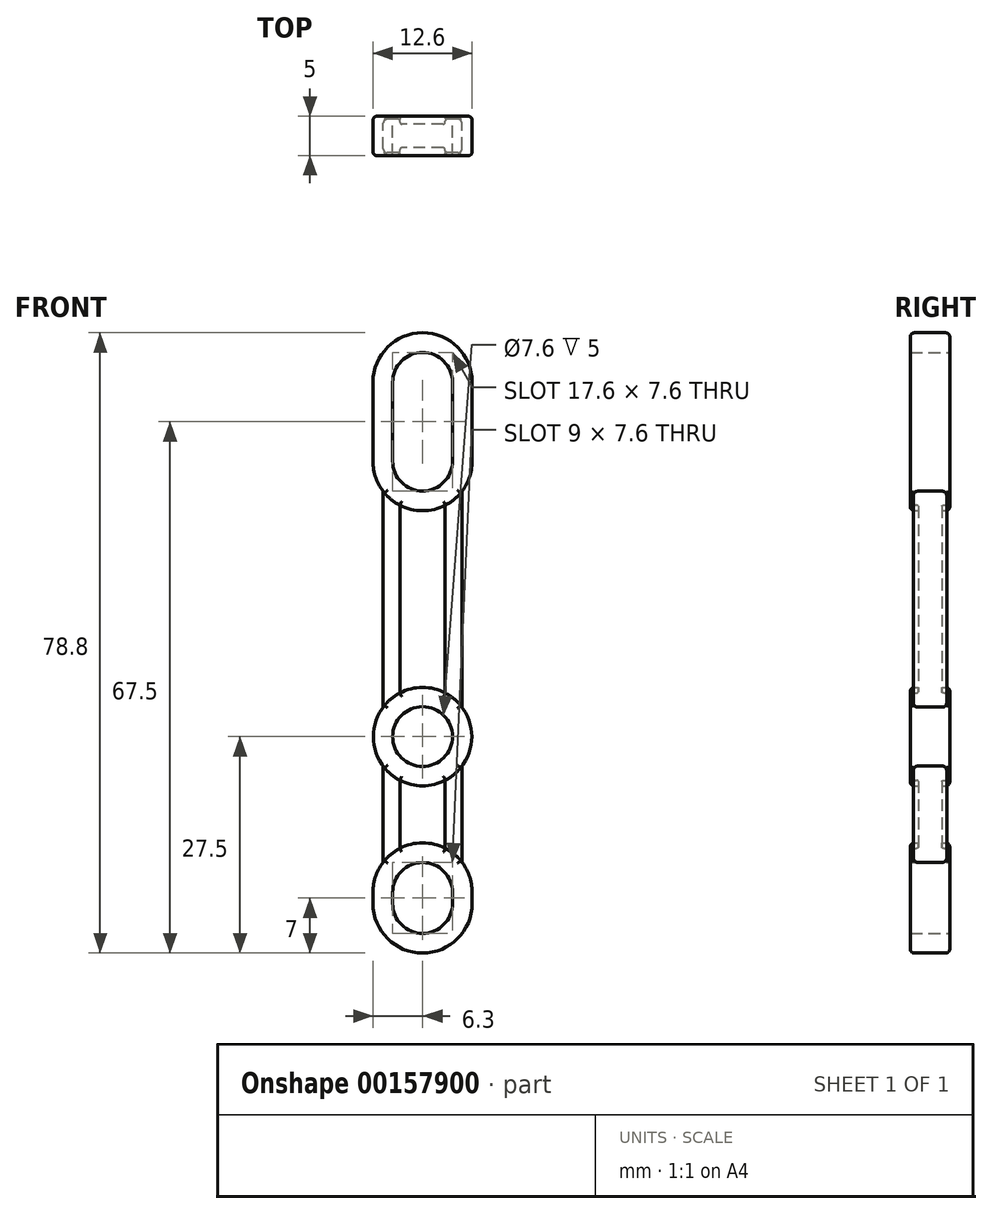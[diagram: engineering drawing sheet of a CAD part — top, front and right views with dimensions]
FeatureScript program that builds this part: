
annotation { "Feature Type Name" : "Feature", "Feature Type Description" : "" }
export const myFeature = defineFeature(function(context is Context, id is Id, definition is map)
    precondition{}
    {
        {
            var Q0;
            Q0=qCreatedBy(makeId("Front.planeOp"),FACE);
            var sketch = newSketch(context, id + "F0", { "sketchPlane" : qUnion([Q0])});
            skPoint(sketch, "E0.end.orphan", {"position": v(0, 40) * mm});
            skLineSegment(sketch, "E1.2", {"start": v(6.3, 45) * mm, "end": v(6.3, 35) * mm});
            skLineSegment(sketch, "E2", {"start": v(3.8, 45) * mm, "end": v(3.8, 35) * mm});
            skLineSegment(sketch, "E3.MirrorCS", {"start": v(-3.8, 45) * mm, "end": v(-3.8, 35) * mm});
            skLineSegment(sketch, "E4.MirrorCS", {"start": v(-6.3, 45) * mm, "end": v(-6.3, 35) * mm});
            skArc(sketch, "E5", {"start": v(-3.8, 35) * mm, "mid": v(0, 31.2) * mm, "end": v(3.8, 35) * mm});
            skArc(sketch, "E6", {"start": v(-6.3, 35) * mm, "mid": v(0, 28.7) * mm, "end": v(6.3, 35) * mm});
            skArc(sketch, "E7.MirrorCS", {"start": v(-6.3, 45) * mm, "mid": v(0, 51.3) * mm, "end": v(6.3, 45) * mm});
            skArc(sketch, "E8.MirrorCS", {"start": v(-3.8, 45) * mm, "mid": v(0, 48.8) * mm, "end": v(3.8, 45) * mm});
            skCircle(sketch, "E9", {"center": v(0, 0) * mm, "radius": 3.8 * mm});
            skCircle(sketch, "E10", {"center": v(0, 0) * mm, "radius": 6.25 * mm});
            skSolve(sketch);
        }
        {
            var Q0;
            Q0=makeQuery(id+"F0.imprint","IMPRINT",FACE,{"disambiguationData":[TD([[makeQuery(id+"F0.imprint","IMPRINT",EDGE,{"derivedFrom":sQuery(id+"F0.wireOp",EDGE,"E1.2")}),-1.0]])]});
            extrude(context, id + "F1", {"entities" : qUnion([Q0]), "depth" : 5 * mm, "symmetric" : true});
        }
        {
            var Q0;
            Q0=qCreatedBy(makeId("Front.planeOp"),FACE);
            var sketch = newSketch(context, id + "F2", { "sketchPlane" : qUnion([Q0])});
            skCircle(sketch, "E11", {"center": v(0, 0) * mm, "radius": 3.8 * mm});
            skCircle(sketch, "E12", {"center": v(0, 0) * mm, "radius": 6.25 * mm});
            skSolve(sketch);
        }
        {
            var Q0;
            Q0 = qSketchRegion(id + "F2", true);
            extrude(context, id + "F3", {"entities" : qUnion([Q0]), "operationType" : NewBodyOperationType.ADD, "depth" : 5 * mm, "symmetric" : true});
        }
        {
            var Q0;
            Q0=qCreatedBy(makeId("Front.planeOp"),FACE);
            var sketch = newSketch(context, id + "F4", { "sketchPlane" : qUnion([Q0])});
            skArc(sketch, "E13", {"start": v(-3.8, -21.2) * mm, "mid": v(0, -25) * mm, "end": v(3.8, -21.2) * mm});
            skLineSegment(sketch, "E14", {"start": v(0, -19.8) * mm, "end": v(0, -20) * mm});
            skLineSegment(sketch, "E15", {"start": v(0, -20) * mm, "end": v(0, -21.2) * mm});
            skArc(sketch, "E16.trimOffspring", {"start": v(3.8, -19.8) * mm, "mid": v(0, -16) * mm, "end": v(-3.8, -19.8) * mm});
            skLineSegment(sketch, "E17", {"start": v(-3.8, -19.8) * mm, "end": v(-3.8, -21.2) * mm});
            skLineSegment(sketch, "E18", {"start": v(3.8, -19.8) * mm, "end": v(3.8, -21.2) * mm});
            skLineSegment(sketch, "E19.0", {"start": v(-6.3, -19.8) * mm, "end": v(-6.3, -21.2) * mm});
            skArc(sketch, "E19.1", {"start": v(6.3, -19.8) * mm, "mid": v(0, -13.5) * mm, "end": v(-6.3, -19.8) * mm});
            skLineSegment(sketch, "E19.2", {"start": v(6.3, -19.8) * mm, "end": v(6.3, -21.2) * mm});
            skArc(sketch, "E19.3", {"start": v(-6.3, -21.2) * mm, "mid": v(0, -27.5) * mm, "end": v(6.3, -21.2) * mm});
            skSolve(sketch);
        }
        {
            var Q0;
            Q0 = qSketchRegion(id + "F4", true);
            extrude(context, id + "F5", {"entities" : qUnion([Q0]), "operationType" : NewBodyOperationType.ADD, "depth" : 5 * mm, "symmetric" : true});
        }
        {
            var Q0;
            Q0=qCreatedBy(makeId("Top.planeOp"),FACE);
            cPlane(context, id + "F6", {"entities" : qUnion([Q0]), "cplaneType" : CPlaneType.OFFSET, "offset" : 20 * mm, "width" : 150 * mm, "height" : 150 * mm});
        }
        {
            var Q0;
            Q0=qCreatedBy(id+"F6.planeOp",FACE);
            var sketch = newSketch(context, id + "F7", { "sketchPlane" : qUnion([Q0])});
            skLineSegment(sketch, "E20.top", {"start": v(-4.5, 2.12) * mm, "end": v(-3.12, 2.12) * mm});
            skLineSegment(sketch, "E21", {"start": v(5, -1.63) * mm, "end": v(5, 1.62) * mm});
            skLineSegment(sketch, "E22", {"start": v(-5, -1.63) * mm, "end": v(-5, 1.62) * mm});
            skLineSegment(sketch, "E23", {"start": v(-4.5, -2.13) * mm, "end": v(-3.12, -2.13) * mm});
            skLineSegment(sketch, "E24.bottom", {"start": v(-2.62, -1.5) * mm, "end": v(2.62, -1.5) * mm});
            skLineSegment(sketch, "E24.top", {"start": v(-2.63, 1.5) * mm, "end": v(2.62, 1.5) * mm});
            skLineSegment(sketch, "E25", {"start": v(-2.88, -1.75) * mm, "end": v(-2.88, -1.88) * mm});
            skLineSegment(sketch, "E26", {"start": v(-2.88, 1.75) * mm, "end": v(-2.88, 1.87) * mm});
            skLineSegment(sketch, "E27", {"start": v(2.87, 1.75) * mm, "end": v(2.87, 1.87) * mm});
            skLineSegment(sketch, "E28", {"start": v(2.88, -1.75) * mm, "end": v(2.88, -1.88) * mm});
            skLineSegment(sketch, "E29.trimOffspring", {"start": v(3.12, -2.13) * mm, "end": v(4.5, -2.13) * mm});
            skLineSegment(sketch, "E30.trimOffspring", {"start": v(3.12, 2.12) * mm, "end": v(4.5, 2.12) * mm});
            skPoint(sketch, "E31.visualSharp", {"position": v(-5, -2.13) * mm});
            skArc(sketch, "E31.filletArc", {"start": v(-5, -1.63) * mm, "mid": v(-4.85, -1.98) * mm, "end": v(-4.5, -2.13) * mm});
            skPoint(sketch, "E32.visualSharp", {"position": v(-5, 2.12) * mm});
            skArc(sketch, "E32.filletArc", {"start": v(-4.5, 2.12) * mm, "mid": v(-4.85, 1.98) * mm, "end": v(-5, 1.62) * mm});
            skPoint(sketch, "E33.visualSharp", {"position": v(5, 2.13) * mm});
            skArc(sketch, "E33.filletArc", {"start": v(5, 1.62) * mm, "mid": v(4.85, 1.98) * mm, "end": v(4.5, 2.12) * mm});
            skPoint(sketch, "E34.visualSharp", {"position": v(5, -2.13) * mm});
            skArc(sketch, "E34.filletArc", {"start": v(4.5, -2.13) * mm, "mid": v(4.85, -1.98) * mm, "end": v(5, -1.63) * mm});
            skPoint(sketch, "E35.visualSharp", {"position": v(2.88, -1.5) * mm});
            skArc(sketch, "E35.filletArc", {"start": v(2.88, -1.75) * mm, "mid": v(2.8, -1.57) * mm, "end": v(2.62, -1.5) * mm});
            skPoint(sketch, "E36.visualSharp", {"position": v(-2.88, -1.5) * mm});
            skArc(sketch, "E36.filletArc", {"start": v(-2.62, -1.5) * mm, "mid": v(-2.8, -1.57) * mm, "end": v(-2.88, -1.75) * mm});
            skPoint(sketch, "E37.visualSharp", {"position": v(-2.88, 1.5) * mm});
            skArc(sketch, "E37.filletArc", {"start": v(-2.88, 1.75) * mm, "mid": v(-2.8, 1.57) * mm, "end": v(-2.63, 1.5) * mm});
            skPoint(sketch, "E38.visualSharp", {"position": v(2.87, 1.5) * mm});
            skArc(sketch, "E38.filletArc", {"start": v(2.62, 1.5) * mm, "mid": v(2.8, 1.57) * mm, "end": v(2.88, 1.75) * mm});
            skPoint(sketch, "E39.visualSharp", {"position": v(2.88, -2.13) * mm});
            skArc(sketch, "E39.filletArc", {"start": v(2.88, -1.88) * mm, "mid": v(2.95, -2.05) * mm, "end": v(3.12, -2.13) * mm});
            skPoint(sketch, "E40.visualSharp", {"position": v(-2.88, -2.13) * mm});
            skArc(sketch, "E40.filletArc", {"start": v(-3.12, -2.13) * mm, "mid": v(-2.95, -2.05) * mm, "end": v(-2.88, -1.88) * mm});
            skPoint(sketch, "E41.visualSharp", {"position": v(-2.88, 2.12) * mm});
            skArc(sketch, "E41.filletArc", {"start": v(-2.88, 1.87) * mm, "mid": v(-2.95, 2.05) * mm, "end": v(-3.12, 2.12) * mm});
            skPoint(sketch, "E42.visualSharp", {"position": v(2.87, 2.12) * mm});
            skArc(sketch, "E42.filletArc", {"start": v(3.12, 2.12) * mm, "mid": v(2.95, 2.05) * mm, "end": v(2.87, 1.87) * mm});
            skSolve(sketch);
        }
        {
            var Q0;
            Q0=makeQuery(id+"F7.imprint","IMPRINT",FACE,{"disambiguationData":[TD([[makeQuery(id+"F7.imprint","IMPRINT",EDGE,{"derivedFrom":sQuery(id+"F7.wireOp",EDGE,"E20.top")}),-1.0]])]});
            var Q1;
            Q1=makeQuery(id+"F1.opExtrude","SWEPT_BODY",BODY,{"disambiguationData":[OSD([sQuery(id+"F0.wireOp",EDGE,"E1.2"),sQuery(id+"F0.wireOp",EDGE,"E2"),sQuery(id+"F0.wireOp",EDGE,"E3.MirrorCS"),sQuery(id+"F0.wireOp",EDGE,"E4.MirrorCS"),sQuery(id+"F0.wireOp",EDGE,"E5"),sQuery(id+"F0.wireOp",EDGE,"E6"),sQuery(id+"F0.wireOp",EDGE,"E7.MirrorCS"),sQuery(id+"F0.wireOp",EDGE,"E8.MirrorCS")])]});
            extrude(context, id + "F8", {"entities" : qUnion([Q0]), "operationType" : NewBodyOperationType.ADD, "endBound" : BoundingType.UP_TO_BODY, "endBoundEntityBody" : qUnion([Q1]), "depth" : 25 * mm});
        }
        {
            var Q0;
            Q0=makeQuery(id+"F8.opExtrude","CAP_FACE",FACE,{"disambiguationData":[OSD([sQuery(id+"F7.wireOp",EDGE,"E20.top"),sQuery(id+"F7.wireOp",EDGE,"E21"),sQuery(id+"F7.wireOp",EDGE,"E22"),sQuery(id+"F7.wireOp",EDGE,"E23"),sQuery(id+"F7.wireOp",EDGE,"E24.bottom"),sQuery(id+"F7.wireOp",EDGE,"E24.top"),sQuery(id+"F7.wireOp",EDGE,"E25"),sQuery(id+"F7.wireOp",EDGE,"E26"),sQuery(id+"F7.wireOp",EDGE,"E27"),sQuery(id+"F7.wireOp",EDGE,"E28"),sQuery(id+"F7.wireOp",EDGE,"E29.trimOffspring"),sQuery(id+"F7.wireOp",EDGE,"E30.trimOffspring"),sQuery(id+"F7.wireOp",EDGE,"E31.filletArc"),sQuery(id+"F7.wireOp",EDGE,"E32.filletArc"),sQuery(id+"F7.wireOp",EDGE,"E33.filletArc"),sQuery(id+"F7.wireOp",EDGE,"E34.filletArc"),sQuery(id+"F7.wireOp",EDGE,"E35.filletArc"),sQuery(id+"F7.wireOp",EDGE,"E36.filletArc"),sQuery(id+"F7.wireOp",EDGE,"E37.filletArc"),sQuery(id+"F7.wireOp",EDGE,"E38.filletArc"),sQuery(id+"F7.wireOp",EDGE,"E39.filletArc"),sQuery(id+"F7.wireOp",EDGE,"E40.filletArc"),sQuery(id+"F7.wireOp",EDGE,"E41.filletArc"),sQuery(id+"F7.wireOp",EDGE,"E42.filletArc")])],"isStart":true});
            var Q1;
            Q1=makeQuery(id+"F3.opExtrude","SWEPT_BODY",BODY,{"disambiguationData":[OSD([sQuery(id+"F2.wireOp",EDGE,"E11"),sQuery(id+"F2.wireOp",EDGE,"E12")])]});
            extrude(context, id + "F9", {"entities" : qUnion([Q0]), "operationType" : NewBodyOperationType.ADD, "endBound" : BoundingType.UP_TO_BODY, "endBoundEntityBody" : qUnion([Q1]), "depth" : 25 * mm});
        }
        {
            var Q0;
            Q0=qCreatedBy(makeId("Top.planeOp"),FACE);
            cPlane(context, id + "F10", {"entities" : qUnion([Q0]), "cplaneType" : CPlaneType.OFFSET, "offset" : 10 * mm, "oppositeDirection" : true, "width" : 150 * mm, "height" : 150 * mm});
        }
        {
            var Q0;
            Q0=qCreatedBy(id+"F10.planeOp",FACE);
            var sketch = newSketch(context, id + "F11", { "sketchPlane" : qUnion([Q0])});
            skLineSegment(sketch, "E43.0", {"start": v(-4.5, 2.12) * mm, "end": v(-3.12, 2.12) * mm});
            skLineSegment(sketch, "E43.1", {"start": v(5, -1.63) * mm, "end": v(5, 1.62) * mm});
            skLineSegment(sketch, "E43.2", {"start": v(-5, -1.63) * mm, "end": v(-5, 1.62) * mm});
            skLineSegment(sketch, "E43.3", {"start": v(-4.5, -2.13) * mm, "end": v(-3.12, -2.13) * mm});
            skLineSegment(sketch, "E43.4", {"start": v(-2.62, -1.5) * mm, "end": v(2.62, -1.5) * mm});
            skLineSegment(sketch, "E43.5", {"start": v(-2.63, 1.5) * mm, "end": v(2.62, 1.5) * mm});
            skLineSegment(sketch, "E43.6", {"start": v(-2.88, -1.75) * mm, "end": v(-2.88, -1.88) * mm});
            skLineSegment(sketch, "E43.7", {"start": v(-2.88, 1.75) * mm, "end": v(-2.88, 1.87) * mm});
            skLineSegment(sketch, "E43.8", {"start": v(2.87, 1.75) * mm, "end": v(2.87, 1.87) * mm});
            skLineSegment(sketch, "E43.9", {"start": v(2.88, -1.75) * mm, "end": v(2.88, -1.88) * mm});
            skLineSegment(sketch, "E43.10", {"start": v(3.12, -2.13) * mm, "end": v(4.5, -2.13) * mm});
            skLineSegment(sketch, "E43.11", {"start": v(3.12, 2.12) * mm, "end": v(4.5, 2.12) * mm});
            skPoint(sketch, "E43.12", {"position": v(-5, -2.13) * mm});
            skArc(sketch, "E43.13", {"start": v(-5, -1.63) * mm, "mid": v(-4.85, -1.98) * mm, "end": v(-4.5, -2.13) * mm});
            skPoint(sketch, "E43.14", {"position": v(-5, 2.12) * mm});
            skArc(sketch, "E43.15", {"start": v(-4.5, 2.12) * mm, "mid": v(-4.85, 1.98) * mm, "end": v(-5, 1.62) * mm});
            skPoint(sketch, "E43.16", {"position": v(5, 2.13) * mm});
            skArc(sketch, "E43.17", {"start": v(5, 1.62) * mm, "mid": v(4.85, 1.98) * mm, "end": v(4.5, 2.12) * mm});
            skPoint(sketch, "E43.18", {"position": v(5, -2.13) * mm});
            skArc(sketch, "E43.19", {"start": v(4.5, -2.13) * mm, "mid": v(4.85, -1.98) * mm, "end": v(5, -1.63) * mm});
            skPoint(sketch, "E43.20", {"position": v(2.88, -1.5) * mm});
            skArc(sketch, "E43.21", {"start": v(2.88, -1.75) * mm, "mid": v(2.8, -1.57) * mm, "end": v(2.62, -1.5) * mm});
            skPoint(sketch, "E43.22", {"position": v(-2.88, -1.5) * mm});
            skArc(sketch, "E43.23", {"start": v(-2.62, -1.5) * mm, "mid": v(-2.8, -1.57) * mm, "end": v(-2.88, -1.75) * mm});
            skPoint(sketch, "E43.24", {"position": v(-2.88, 1.5) * mm});
            skArc(sketch, "E43.25", {"start": v(-2.88, 1.75) * mm, "mid": v(-2.8, 1.57) * mm, "end": v(-2.63, 1.5) * mm});
            skPoint(sketch, "E43.26", {"position": v(2.87, 1.5) * mm});
            skArc(sketch, "E43.27", {"start": v(2.62, 1.5) * mm, "mid": v(2.8, 1.57) * mm, "end": v(2.88, 1.75) * mm});
            skPoint(sketch, "E43.28", {"position": v(2.88, -2.13) * mm});
            skArc(sketch, "E43.29", {"start": v(2.88, -1.88) * mm, "mid": v(2.95, -2.05) * mm, "end": v(3.12, -2.13) * mm});
            skPoint(sketch, "E43.30", {"position": v(-2.88, -2.13) * mm});
            skArc(sketch, "E43.31", {"start": v(-3.12, -2.13) * mm, "mid": v(-2.95, -2.05) * mm, "end": v(-2.88, -1.88) * mm});
            skPoint(sketch, "E43.32", {"position": v(-2.88, 2.12) * mm});
            skArc(sketch, "E43.33", {"start": v(-2.88, 1.87) * mm, "mid": v(-2.95, 2.05) * mm, "end": v(-3.12, 2.12) * mm});
            skPoint(sketch, "E43.34", {"position": v(2.87, 2.12) * mm});
            skArc(sketch, "E43.35", {"start": v(3.12, 2.12) * mm, "mid": v(2.95, 2.05) * mm, "end": v(2.87, 1.87) * mm});
            skLineSegment(sketch, "E43.36", {"start": v(-2.62, -1.5) * mm, "end": v(2.62, -1.5) * mm});
            skSolve(sketch);
        }
        {
            var Q0;
            Q0 = qSketchRegion(id + "F11", true);
            var Q1;
            Q1=makeQuery(id+"F3.opExtrude","SWEPT_FACE",FACE,{"disambiguationData":[OSD([sQuery(id+"F2.wireOp",EDGE,"E12")])]});
            var Q2;
            Q2=makeQuery(id+"F3.opExtrude","SWEPT_BODY",BODY,{"disambiguationData":[OSD([sQuery(id+"F2.wireOp",EDGE,"E11"),sQuery(id+"F2.wireOp",EDGE,"E12")])]});
            extrude(context, id + "F12", {"entities" : qUnion([Q0]), "operationType" : NewBodyOperationType.ADD, "endBound" : BoundingType.UP_TO_SURFACE, "endBoundEntityFace" : qUnion([Q1]), "endBoundEntityBody" : qUnion([Q2]), "depth" : 25 * mm});
        }
        {
            var Q0;
            Q0=makeQuery(id+"F12.opExtrude","CAP_FACE",FACE,{"disambiguationData":[OSD([sQuery(id+"F11.wireOp",EDGE,"E43.0"),sQuery(id+"F11.wireOp",EDGE,"E43.1"),sQuery(id+"F11.wireOp",EDGE,"E43.2"),sQuery(id+"F11.wireOp",EDGE,"E43.3"),sQuery(id+"F11.wireOp",EDGE,"E43.5"),sQuery(id+"F11.wireOp",EDGE,"E43.6"),sQuery(id+"F11.wireOp",EDGE,"E43.7"),sQuery(id+"F11.wireOp",EDGE,"E43.8"),sQuery(id+"F11.wireOp",EDGE,"E43.9"),sQuery(id+"F11.wireOp",EDGE,"E43.10"),sQuery(id+"F11.wireOp",EDGE,"E43.11"),sQuery(id+"F11.wireOp",EDGE,"E43.13"),sQuery(id+"F11.wireOp",EDGE,"E43.15"),sQuery(id+"F11.wireOp",EDGE,"E43.17"),sQuery(id+"F11.wireOp",EDGE,"E43.19"),sQuery(id+"F11.wireOp",EDGE,"E43.21"),sQuery(id+"F11.wireOp",EDGE,"E43.23"),sQuery(id+"F11.wireOp",EDGE,"E43.25"),sQuery(id+"F11.wireOp",EDGE,"E43.27"),sQuery(id+"F11.wireOp",EDGE,"E43.29"),sQuery(id+"F11.wireOp",EDGE,"E43.31"),sQuery(id+"F11.wireOp",EDGE,"E43.33"),sQuery(id+"F11.wireOp",EDGE,"E43.35"),sQuery(id+"F11.wireOp",EDGE,"E43.36")])],"isStart":true});
            var Q1;
            Q1=makeQuery(id+"F5.opExtrude","SWEPT_BODY",BODY,{"disambiguationData":[OSD([sQuery(id+"F4.wireOp",EDGE,"E13"),sQuery(id+"F4.wireOp",EDGE,"E16.trimOffspring"),sQuery(id+"F4.wireOp",EDGE,"E17"),sQuery(id+"F4.wireOp",EDGE,"E18"),sQuery(id+"F4.wireOp",EDGE,"E19.0"),sQuery(id+"F4.wireOp",EDGE,"E19.1"),sQuery(id+"F4.wireOp",EDGE,"E19.2"),sQuery(id+"F4.wireOp",EDGE,"E19.3")])]});
            extrude(context, id + "F13", {"entities" : qUnion([Q0]), "operationType" : NewBodyOperationType.ADD, "endBound" : BoundingType.UP_TO_BODY, "endBoundEntityBody" : qUnion([Q1]), "depth" : 25 * mm});
        }
        {
            var Q0;
            Q0=makeQuery(id+"F3.opExtrude","CAP_EDGE",EDGE,{"disambiguationData":[OSD([sQuery(id+"F2.wireOp",EDGE,"E12")])],"isStart":false});
            var Q1;
            Q1=makeQuery(id+"F3.opExtrude","CAP_EDGE",EDGE,{"disambiguationData":[OSD([sQuery(id+"F2.wireOp",EDGE,"E12")])],"isStart":true});
            var Q2;
            Q2=makeQuery(id+"F1.opExtrude","CAP_EDGE",EDGE,{"disambiguationData":[OSD([sQuery(id+"F0.wireOp",EDGE,"E7.MirrorCS")])],"isStart":false});
            var Q3;
            Q3=makeQuery(id+"F1.opExtrude","CAP_EDGE",EDGE,{"disambiguationData":[OSD([sQuery(id+"F0.wireOp",EDGE,"E7.MirrorCS")])],"isStart":true});
            var Q4;
            Q4=makeQuery(id+"F5.opExtrude","CAP_EDGE",EDGE,{"disambiguationData":[OSD([sQuery(id+"F4.wireOp",EDGE,"E19.1")])],"isStart":false});
            var Q5;
            Q5=makeQuery(id+"F5.opExtrude","CAP_EDGE",EDGE,{"disambiguationData":[OSD([sQuery(id+"F4.wireOp",EDGE,"E19.1")])],"isStart":true});
            fillet(context, id + "F14", {"entities" : qUnion([Q0, Q1, Q2, Q3, Q4, Q5]), "radius" : 0.5 * mm, "tangentPropagation" : true, "allowEdgeOverflow" : false});
        }
    });
